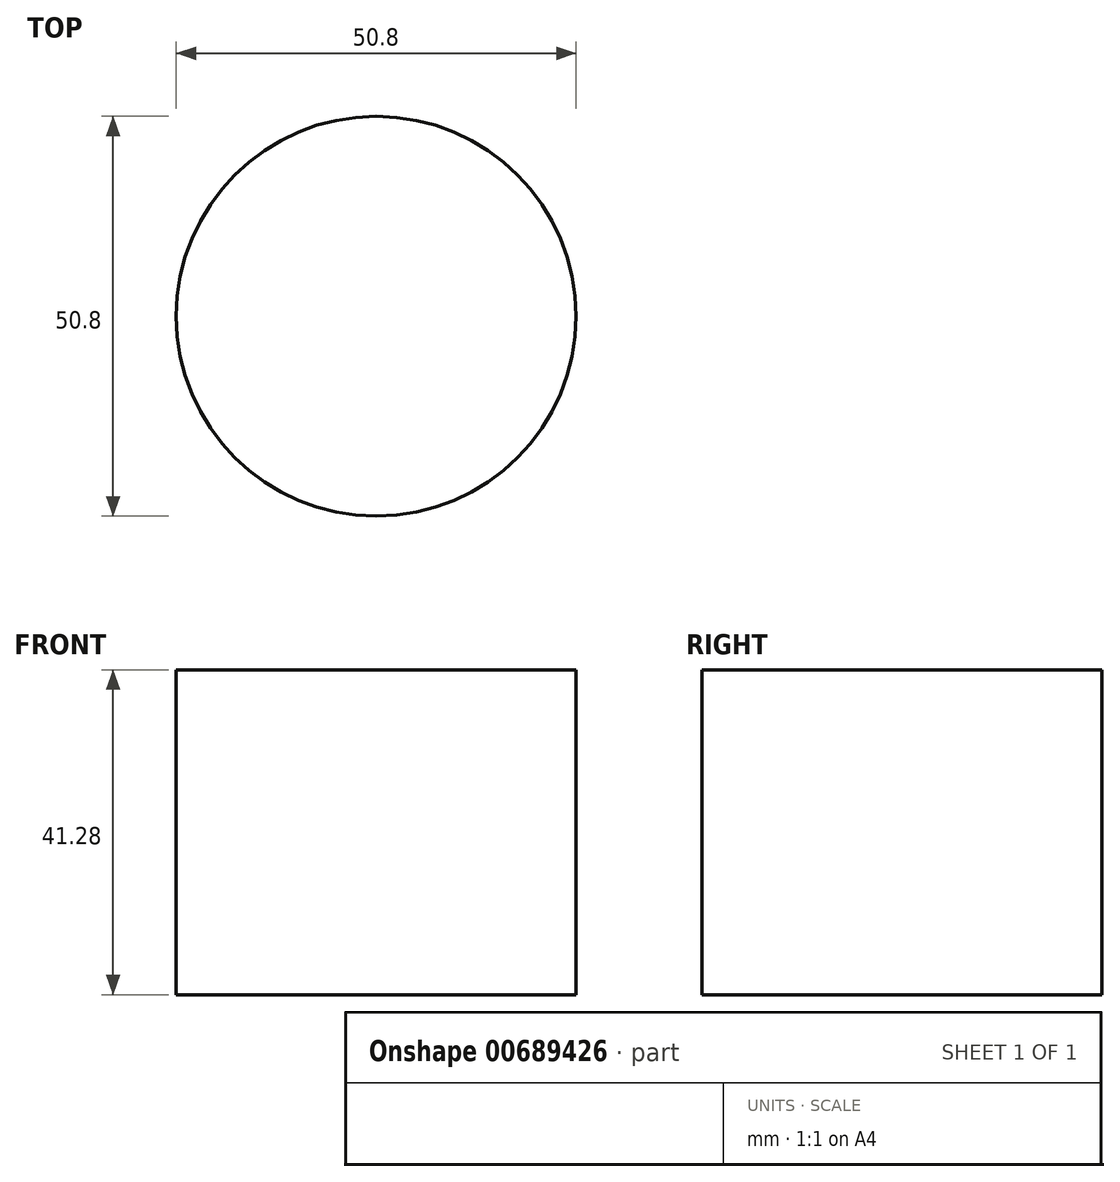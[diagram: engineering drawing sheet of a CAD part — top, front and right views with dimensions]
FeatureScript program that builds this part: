
annotation { "Feature Type Name" : "Feature", "Feature Type Description" : "" }
export const myFeature = defineFeature(function(context is Context, id is Id, definition is map)
    precondition{}
    {
        {
            var Q0;
            Q0=qCreatedBy(makeId("Top.planeOp"),FACE);
            var sketch = newSketch(context, id + "F0", { "sketchPlane" : qUnion([Q0])});
            skCircle(sketch, "E0", {"center": v(0, 0) * mm, "radius": 25.4 * mm});
            skSolve(sketch);
        }
        {
            var Q0;
            Q0=makeQuery(id+"F0.imprint","IMPRINT",FACE,{"disambiguationData":[TD([[makeQuery(id+"F0.imprint","IMPRINT",EDGE,{"derivedFrom":sQuery(id+"F0.wireOp",EDGE,"E0")}),1.0]])]});
            extrude(context, id + "F1", {"entities" : qUnion([Q0]), "depth" : 41.27 * mm, "offsetDistance" : 25.4 * mm});
        }
    });
